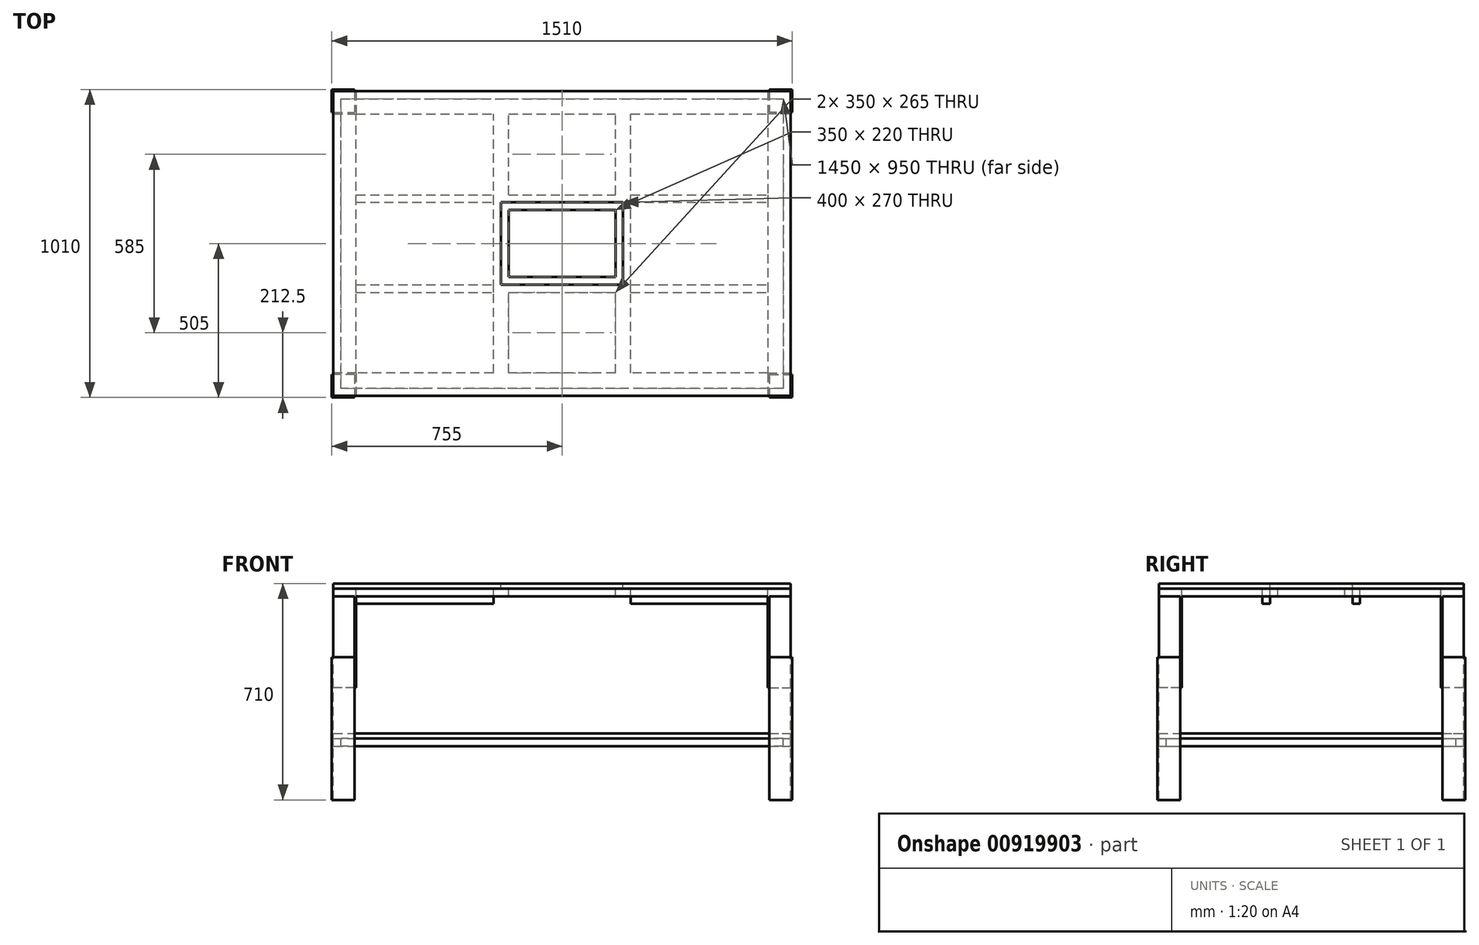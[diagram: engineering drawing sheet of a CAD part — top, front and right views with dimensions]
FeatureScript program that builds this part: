
annotation { "Feature Type Name" : "Feature", "Feature Type Description" : "" }
export const myFeature = defineFeature(function(context is Context, id is Id, definition is map)
    precondition{}
    {
        {
            var Q0;
            Q0=qCreatedBy(makeId("Top.planeOp"),FACE);
            var sketch = newSketch(context, id + "F0", { "sketchPlane" : qUnion([Q0])});
            skLineSegment(sketch, "E0.bottom", {"start": v(750, 500) * mm, "end": v(-750, 500) * mm});
            skLineSegment(sketch, "E0.top", {"start": v(750, -500) * mm, "end": v(-750, -500) * mm});
            skLineSegment(sketch, "E0.left", {"start": v(750, 500) * mm, "end": v(750, -500) * mm});
            skLineSegment(sketch, "E0.right", {"start": v(-750, 500) * mm, "end": v(-750, -500) * mm});
            skPoint(sketch, "E0.middle", {"position": v(0, 0) * mm});
            skSolve(sketch);
        }
        {
            var Q0;
            Q0=makeQuery(id+"F0.imprint","IMPRINT",FACE,{"disambiguationData":[TD([[makeQuery(id+"F0.imprint","IMPRINT",EDGE,{"derivedFrom":sQuery(id+"F0.wireOp",EDGE,"E0.bottom")}),1.0]])]});
            extrude(context, id + "F1", {"entities" : qUnion([Q0]), "depth" : 17 * mm, "offsetDistance" : 25 * mm});
        }
        {
            var Q0;
            Q0=makeQuery(id+"F1.opExtrude","CAP_FACE",FACE,{"disambiguationData":[OSD([sQuery(id+"F0.wireOp",EDGE,"E0.bottom"),sQuery(id+"F0.wireOp",EDGE,"E0.top"),sQuery(id+"F0.wireOp",EDGE,"E0.left"),sQuery(id+"F0.wireOp",EDGE,"E0.right")])],"isStart":true});
            var sketch = newSketch(context, id + "F2", { "sketchPlane" : qUnion([Q0])});
            skLineSegment(sketch, "E1.0.0", {"start": v(750, 500) * mm, "end": v(-750, 500) * mm});
            skLineSegment(sketch, "E1.0.1", {"start": v(-750, 500) * mm, "end": v(-750, -500) * mm});
            skLineSegment(sketch, "E1.0.2", {"start": v(-750, -500) * mm, "end": v(750, -500) * mm});
            skLineSegment(sketch, "E1.0.3", {"start": v(750, -500) * mm, "end": v(750, 500) * mm});
            skLineSegment(sketch, "E2.0", {"start": v(675, 425) * mm, "end": v(-675, 425) * mm});
            skLineSegment(sketch, "E2.1", {"start": v(675, -425) * mm, "end": v(675, 425) * mm});
            skLineSegment(sketch, "E2.2", {"start": v(-675, -425) * mm, "end": v(675, -425) * mm});
            skLineSegment(sketch, "E2.3", {"start": v(-675, 425) * mm, "end": v(-675, -425) * mm});
            skLineSegment(sketch, "E3", {"start": v(-175, 425) * mm, "end": v(-175, -425) * mm});
            skLineSegment(sketch, "E4", {"start": v(175, 425) * mm, "end": v(175, -425) * mm});
            skLineSegment(sketch, "E5", {"start": v(0, 425) * mm, "end": v(0, -425) * mm, "construction": true});
            skLineSegment(sketch, "E6", {"start": v(-675, 0) * mm, "end": v(675, 0) * mm, "construction": true});
            skLineSegment(sketch, "E7.0", {"start": v(225, 425) * mm, "end": v(225, -425) * mm});
            skLineSegment(sketch, "E8.0", {"start": v(-225, 425) * mm, "end": v(-225, -425) * mm});
            skLineSegment(sketch, "E9", {"start": v(-175, 110) * mm, "end": v(175, 110) * mm});
            skLineSegment(sketch, "E10", {"start": v(-175, -110) * mm, "end": v(175, -110) * mm});
            skLineSegment(sketch, "E11.0", {"start": v(-175, 160) * mm, "end": v(175, 160) * mm});
            skLineSegment(sketch, "E12.0", {"start": v(-175, -160) * mm, "end": v(175, -160) * mm});
            skLineSegment(sketch, "E13", {"start": v(-675, 160) * mm, "end": v(-225, 160) * mm});
            skLineSegment(sketch, "E14", {"start": v(-675, -160) * mm, "end": v(-225, -160) * mm});
            skLineSegment(sketch, "E15.0", {"start": v(-675, 135) * mm, "end": v(-225, 135) * mm});
            skLineSegment(sketch, "E16.0", {"start": v(-675, -135) * mm, "end": v(-225, -135) * mm});
            skLineSegment(sketch, "E17.trimOffspring", {"start": v(225, 160) * mm, "end": v(675, 160) * mm});
            skLineSegment(sketch, "E18.trimOffspring", {"start": v(225, 135) * mm, "end": v(675, 135) * mm});
            skLineSegment(sketch, "E19.trimOffspring", {"start": v(225, -135) * mm, "end": v(675, -135) * mm});
            skLineSegment(sketch, "E20.trimOffspring", {"start": v(225, -160) * mm, "end": v(675, -160) * mm});
            skSolve(sketch);
        }
        {
            var Q0;
            Q0=makeQuery(id+"F2.imprint","IMPRINT",FACE,{"disambiguationData":[TD([[makeQuery(id+"F2.imprint","IMPRINT",EDGE,{"derivedFrom":sQuery(id+"F2.wireOp",EDGE,"E1.0.0")}),1.0]])]});
            var Q1;
            {var subQ3=sQuery(id+"F2.wireOp",EDGE,"E2.0");var subQ6=sQuery(id+"F2.wireOp",EDGE,"E3");var subQ11=makeQuery(id+"F2.imprint","INTERSECT",VERTEX,{"derivedFrom":[subQ3,subQ6]});Q1=makeQuery(id+"F2.imprint","IMPRINT",FACE,{"disambiguationData":[TD([[makeQuery(id+"F2.imprint","IMPRINT",EDGE,{"disambiguationData":[TD([[subQ11,-1.0]])],"derivedFrom":subQ3}),1.0]])]});}
            var Q2;
            {var subQ4=sQuery(id+"F2.wireOp",EDGE,"E2.0");var subQ6=sQuery(id+"F2.wireOp",EDGE,"E4");var subQ12=makeQuery(id+"F2.imprint","INTERSECT",VERTEX,{"derivedFrom":[subQ4,subQ6]});Q2=makeQuery(id+"F2.imprint","IMPRINT",FACE,{"disambiguationData":[TD([[makeQuery(id+"F2.imprint","IMPRINT",EDGE,{"disambiguationData":[TD([[subQ12,1.0]])],"derivedFrom":subQ4}),1.0]])]});}
            var Q3;
            {var subQ0=sQuery(id+"F2.wireOp",EDGE,"E9");Q3=makeQuery(id+"F2.imprint","IMPRINT",FACE,{"disambiguationData":[TD([[makeQuery(id+"F2.imprint","IMPRINT",EDGE,{"derivedFrom":subQ0}),1.0]])]});}
            var Q4;
            {var subQ0=sQuery(id+"F2.wireOp",EDGE,"E10");Q4=makeQuery(id+"F2.imprint","IMPRINT",FACE,{"disambiguationData":[TD([[makeQuery(id+"F2.imprint","IMPRINT",EDGE,{"derivedFrom":subQ0}),-1.0]])]});}
            extrude(context, id + "F3", {"entities" : qUnion([Q0, Q1, Q2, Q3, Q4]), "depth" : 25 * mm, "offsetDistance" : 25 * mm});
        }
        {
            var Q0;
            {var subQ0=sQuery(id+"F2.wireOp",EDGE,"E13");Q0=makeQuery(id+"F2.imprint","IMPRINT",FACE,{"disambiguationData":[TD([[makeQuery(id+"F2.imprint","IMPRINT",EDGE,{"derivedFrom":subQ0}),-1.0]])]});}
            var Q1;
            {var subQ0=sQuery(id+"F2.wireOp",EDGE,"E14");Q1=makeQuery(id+"F2.imprint","IMPRINT",FACE,{"disambiguationData":[TD([[makeQuery(id+"F2.imprint","IMPRINT",EDGE,{"derivedFrom":subQ0}),1.0]])]});}
            var Q2;
            {var subQ0=sQuery(id+"F2.wireOp",EDGE,"E17.trimOffspring");Q2=makeQuery(id+"F2.imprint","IMPRINT",FACE,{"disambiguationData":[TD([[makeQuery(id+"F2.imprint","IMPRINT",EDGE,{"derivedFrom":subQ0}),-1.0]])]});}
            var Q3;
            {var subQ0=sQuery(id+"F2.wireOp",EDGE,"E19.trimOffspring");Q3=makeQuery(id+"F2.imprint","IMPRINT",FACE,{"disambiguationData":[TD([[makeQuery(id+"F2.imprint","IMPRINT",EDGE,{"derivedFrom":subQ0}),-1.0]])]});}
            extrude(context, id + "F4", {"entities" : qUnion([Q0, Q1, Q2, Q3]), "depth" : 50 * mm, "offsetDistance" : 25 * mm});
        }
        {
            var Q0;
            Q0=makeQuery(id+"F1.opExtrude","CAP_FACE",FACE,{"disambiguationData":[OSD([sQuery(id+"F0.wireOp",EDGE,"E0.bottom"),sQuery(id+"F0.wireOp",EDGE,"E0.top"),sQuery(id+"F0.wireOp",EDGE,"E0.left"),sQuery(id+"F0.wireOp",EDGE,"E0.right")])],"isStart":false});
            var sketch = newSketch(context, id + "F5", { "sketchPlane" : qUnion([Q0])});
            skLineSegment(sketch, "E21.bottom", {"start": v(200, 135) * mm, "end": v(-200, 135) * mm});
            skLineSegment(sketch, "E21.top", {"start": v(200, -135) * mm, "end": v(-200, -135) * mm});
            skLineSegment(sketch, "E21.left", {"start": v(200, 135) * mm, "end": v(200, -135) * mm});
            skLineSegment(sketch, "E21.right", {"start": v(-200, 135) * mm, "end": v(-200, -135) * mm});
            skPoint(sketch, "E21.middle", {"position": v(0, 0) * mm});
            skSolve(sketch);
        }
        {
            var Q0;
            Q0=makeQuery(id+"F5.imprint","IMPRINT",FACE,{"disambiguationData":[TD([[makeQuery(id+"F5.imprint","IMPRINT",EDGE,{"derivedFrom":sQuery(id+"F5.wireOp",EDGE,"E21.bottom")}),1.0]])]});
            var Q1;
            {var subQ0=sQuery(id+"F2.wireOp",EDGE,"E2.1");Q1=makeQuery(id+"F3.boolean.opBoolean","SPLIT",FACE,{"disambiguationData":[TD([makeQuery(id+"F3.opExtrude","SWEPT_FACE",FACE,{"disambiguationData":[OSD([subQ0])]})])],"derivedFrom":makeQuery(id+"F1.opExtrude","CAP_FACE",FACE,{"disambiguationData":[OSD([sQuery(id+"F0.wireOp",EDGE,"E0.bottom"),sQuery(id+"F0.wireOp",EDGE,"E0.top"),sQuery(id+"F0.wireOp",EDGE,"E0.left"),sQuery(id+"F0.wireOp",EDGE,"E0.right")])],"isStart":true})});}
            extrude(context, id + "F6", {"entities" : qUnion([Q0]), "operationType" : NewBodyOperationType.REMOVE, "endBound" : BoundingType.UP_TO_SURFACE, "oppositeDirection" : true, "depth" : 25 * mm, "endBoundEntityFace" : qUnion([Q1]), "offsetDistance" : 25 * mm});
        }
        {
            var Q0;
            Q0=makeQuery(id+"F3.opExtrude","CAP_FACE",FACE,{"disambiguationData":[OSD([sQuery(id+"F2.wireOp",EDGE,"E1.0.0"),sQuery(id+"F2.wireOp",EDGE,"E1.0.1"),sQuery(id+"F2.wireOp",EDGE,"E1.0.2"),sQuery(id+"F2.wireOp",EDGE,"E1.0.3"),sQuery(id+"F2.wireOp",EDGE,"E2.0"),sQuery(id+"F2.wireOp",EDGE,"E2.1"),sQuery(id+"F2.wireOp",EDGE,"E2.2"),sQuery(id+"F2.wireOp",EDGE,"E2.3"),sQuery(id+"F2.wireOp",EDGE,"E3"),sQuery(id+"F2.wireOp",EDGE,"E4"),sQuery(id+"F2.wireOp",EDGE,"E7.0"),sQuery(id+"F2.wireOp",EDGE,"E8.0"),sQuery(id+"F2.wireOp",EDGE,"E9"),sQuery(id+"F2.wireOp",EDGE,"E10"),sQuery(id+"F2.wireOp",EDGE,"E11.0"),sQuery(id+"F2.wireOp",EDGE,"E12.0")])],"isStart":false});
            var sketch = newSketch(context, id + "F7", { "sketchPlane" : qUnion([Q0])});
            skLineSegment(sketch, "E22.bottom", {"start": v(-675, 425) * mm, "end": v(-750, 425) * mm});
            skLineSegment(sketch, "E22.top", {"start": v(-675, 500) * mm, "end": v(-750, 500) * mm});
            skLineSegment(sketch, "E22.left", {"start": v(-675, 425) * mm, "end": v(-675, 500) * mm});
            skLineSegment(sketch, "E22.right", {"start": v(-750, 425) * mm, "end": v(-750, 500) * mm});
            skLineSegment(sketch, "E23.bottom", {"start": v(675, 425) * mm, "end": v(750, 425) * mm});
            skLineSegment(sketch, "E23.top", {"start": v(675, 500) * mm, "end": v(750, 500) * mm});
            skLineSegment(sketch, "E23.left", {"start": v(675, 425) * mm, "end": v(675, 500) * mm});
            skLineSegment(sketch, "E23.right", {"start": v(750, 425) * mm, "end": v(750, 500) * mm});
            skLineSegment(sketch, "E24.bottom", {"start": v(-750, -500) * mm, "end": v(-675, -500) * mm});
            skLineSegment(sketch, "E24.top", {"start": v(-750, -425) * mm, "end": v(-675, -425) * mm});
            skLineSegment(sketch, "E24.left", {"start": v(-750, -500) * mm, "end": v(-750, -425) * mm});
            skLineSegment(sketch, "E24.right", {"start": v(-675, -500) * mm, "end": v(-675, -425) * mm});
            skLineSegment(sketch, "E25.bottom", {"start": v(750, -500) * mm, "end": v(675, -500) * mm});
            skLineSegment(sketch, "E25.top", {"start": v(750, -425) * mm, "end": v(675, -425) * mm});
            skLineSegment(sketch, "E25.left", {"start": v(750, -500) * mm, "end": v(750, -425) * mm});
            skLineSegment(sketch, "E25.right", {"start": v(675, -500) * mm, "end": v(675, -425) * mm});
            skLineSegment(sketch, "E26.0", {"start": v(-680, 430) * mm, "end": v(-680, 500) * mm});
            skLineSegment(sketch, "E26.1", {"start": v(-680, 430) * mm, "end": v(-750, 430) * mm});
            skLineSegment(sketch, "E27.0", {"start": v(680, 430) * mm, "end": v(680, 500) * mm});
            skLineSegment(sketch, "E27.1", {"start": v(680, 430) * mm, "end": v(750, 430) * mm});
            skLineSegment(sketch, "E28.0", {"start": v(680, -500) * mm, "end": v(680, -430) * mm});
            skLineSegment(sketch, "E28.1", {"start": v(750, -430) * mm, "end": v(680, -430) * mm});
            skLineSegment(sketch, "E29.0", {"start": v(-680, -500) * mm, "end": v(-680, -430) * mm});
            skLineSegment(sketch, "E29.1", {"start": v(-750, -430) * mm, "end": v(-680, -430) * mm});
            skSolve(sketch);
        }
        {
            var Q0;
            {var subQ1=sQuery(id+"F7.wireOp",EDGE,"E24.top");Q0=makeQuery(id+"F7.imprint","IMPRINT",FACE,{"disambiguationData":[TD([[makeQuery(id+"F7.imprint","IMPRINT",EDGE,{"derivedFrom":subQ1}),-1.0]])]});}
            var Q1;
            {var subQ1=sQuery(id+"F7.wireOp",EDGE,"E22.bottom");Q1=makeQuery(id+"F7.imprint","IMPRINT",FACE,{"disambiguationData":[TD([[makeQuery(id+"F7.imprint","IMPRINT",EDGE,{"derivedFrom":subQ1}),-1.0]])]});}
            var Q2;
            {var subQ1=sQuery(id+"F7.wireOp",EDGE,"E23.bottom");Q2=makeQuery(id+"F7.imprint","IMPRINT",FACE,{"disambiguationData":[TD([[makeQuery(id+"F7.imprint","IMPRINT",EDGE,{"derivedFrom":subQ1}),1.0]])]});}
            var Q3;
            {var subQ2=sQuery(id+"F7.wireOp",EDGE,"E25.top");Q3=makeQuery(id+"F7.imprint","IMPRINT",FACE,{"disambiguationData":[TD([[makeQuery(id+"F7.imprint","IMPRINT",EDGE,{"derivedFrom":subQ2}),1.0]])]});}
            extrude(context, id + "F8", {"entities" : qUnion([Q0, Q1, Q2, Q3]), "operationType" : NewBodyOperationType.ADD, "depth" : 300 * mm, "offsetDistance" : 25 * mm});
        }
        {
            var Q0;
            Q0=makeQuery(id+"F8.opExtrude","CAP_FACE",FACE,{"disambiguationData":[OSD([sQuery(id+"F7.wireOp",EDGE,"E23.bottom"),sQuery(id+"F7.wireOp",EDGE,"E23.top"),sQuery(id+"F7.wireOp",EDGE,"E23.left"),sQuery(id+"F7.wireOp",EDGE,"E23.right"),sQuery(id+"F7.wireOp",EDGE,"E27.0"),sQuery(id+"F7.wireOp",EDGE,"E27.1")])],"isStart":false});
            cPlane(context, id + "F9", {"entities" : qUnion([Q0]), "cplaneType" : CPlaneType.OFFSET, "offset" : 100 * mm, "oppositeDirection" : true, "width" : 150 * mm, "height" : 150 * mm});
        }
        {
            var Q0;
            Q0=qCreatedBy(id+"F9.planeOp",FACE);
            var sketch = newSketch(context, id + "F10", { "sketchPlane" : qUnion([Q0])});
            skLineSegment(sketch, "E30.0.0", {"start": v(750, 430) * mm, "end": v(680, 430) * mm});
            skLineSegment(sketch, "E30.0.1", {"start": v(680, 430) * mm, "end": v(680, 500) * mm});
            skLineSegment(sketch, "E30.0.2", {"start": v(680, 500) * mm, "end": v(675, 500) * mm});
            skLineSegment(sketch, "E30.0.3", {"start": v(675, 500) * mm, "end": v(675, 425) * mm});
            skLineSegment(sketch, "E30.0.4", {"start": v(675, 425) * mm, "end": v(750, 425) * mm});
            skLineSegment(sketch, "E30.0.5", {"start": v(750, 425) * mm, "end": v(750, 430) * mm});
            skLineSegment(sketch, "E31", {"start": v(680, 500) * mm, "end": v(750, 500) * mm});
            skLineSegment(sketch, "E32", {"start": v(750, 500) * mm, "end": v(750, 430) * mm});
            skLineSegment(sketch, "E33", {"start": v(750, 430) * mm, "end": v(755, 430) * mm});
            skLineSegment(sketch, "E34", {"start": v(755, 430) * mm, "end": v(755, 505) * mm});
            skLineSegment(sketch, "E35", {"start": v(755, 505) * mm, "end": v(680, 505) * mm});
            skLineSegment(sketch, "E36", {"start": v(680, 505) * mm, "end": v(680, 500) * mm});
            skLineSegment(sketch, "E37.0.0", {"start": v(-680, 500) * mm, "end": v(-680, 430) * mm});
            skLineSegment(sketch, "E37.0.1", {"start": v(-680, 430) * mm, "end": v(-750, 430) * mm});
            skLineSegment(sketch, "E37.0.2", {"start": v(-750, 430) * mm, "end": v(-750, 425) * mm});
            skLineSegment(sketch, "E37.0.3", {"start": v(-750, 425) * mm, "end": v(-675, 425) * mm});
            skLineSegment(sketch, "E37.0.4", {"start": v(-675, 425) * mm, "end": v(-675, 500) * mm});
            skLineSegment(sketch, "E37.0.5", {"start": v(-675, 500) * mm, "end": v(-680, 500) * mm});
            skPoint(sketch, "E38.0", {"position": v(-750, 500) * mm});
            skLineSegment(sketch, "E39", {"start": v(-680, 500) * mm, "end": v(-750, 500) * mm});
            skLineSegment(sketch, "E40", {"start": v(-750, 500) * mm, "end": v(-750, 430) * mm});
            skLineSegment(sketch, "E41", {"start": v(-750, 430) * mm, "end": v(-755, 430) * mm});
            skLineSegment(sketch, "E42", {"start": v(-755, 430) * mm, "end": v(-755, 505) * mm});
            skLineSegment(sketch, "E43", {"start": v(-755, 505) * mm, "end": v(-680, 505) * mm});
            skLineSegment(sketch, "E44", {"start": v(-680, 505) * mm, "end": v(-680, 500) * mm});
            skLineSegment(sketch, "E45", {"start": v(-750, 500) * mm, "end": v(-680, 500) * mm});
            skLineSegment(sketch, "E46.0.0", {"start": v(-750, -425) * mm, "end": v(-750, -430) * mm});
            skLineSegment(sketch, "E46.0.1", {"start": v(-750, -430) * mm, "end": v(-680, -430) * mm});
            skLineSegment(sketch, "E46.0.2", {"start": v(-680, -430) * mm, "end": v(-680, -500) * mm});
            skLineSegment(sketch, "E46.0.3", {"start": v(-680, -500) * mm, "end": v(-675, -500) * mm});
            skLineSegment(sketch, "E46.0.4", {"start": v(-675, -500) * mm, "end": v(-675, -425) * mm});
            skLineSegment(sketch, "E46.0.5", {"start": v(-675, -425) * mm, "end": v(-750, -425) * mm});
            skPoint(sketch, "E47.0", {"position": v(-750, -500) * mm});
            skLineSegment(sketch, "E48", {"start": v(-750, -430) * mm, "end": v(-750, -500) * mm});
            skLineSegment(sketch, "E49", {"start": v(-750, -500) * mm, "end": v(-680, -500) * mm});
            skLineSegment(sketch, "E50", {"start": v(-680, -500) * mm, "end": v(-680, -505) * mm});
            skLineSegment(sketch, "E51", {"start": v(-680, -505) * mm, "end": v(-755, -505) * mm});
            skLineSegment(sketch, "E52", {"start": v(-755, -505) * mm, "end": v(-755, -430) * mm});
            skLineSegment(sketch, "E53", {"start": v(-755, -430) * mm, "end": v(-750, -430) * mm});
            skLineSegment(sketch, "E54.0.0", {"start": v(680, -430) * mm, "end": v(750, -430) * mm});
            skLineSegment(sketch, "E54.0.1", {"start": v(750, -430) * mm, "end": v(750, -425) * mm});
            skLineSegment(sketch, "E54.0.2", {"start": v(750, -425) * mm, "end": v(675, -425) * mm});
            skLineSegment(sketch, "E54.0.3", {"start": v(675, -425) * mm, "end": v(675, -500) * mm});
            skLineSegment(sketch, "E54.0.4", {"start": v(675, -500) * mm, "end": v(680, -500) * mm});
            skLineSegment(sketch, "E54.0.5", {"start": v(680, -500) * mm, "end": v(680, -430) * mm});
            skPoint(sketch, "E55.0", {"position": v(750, -500) * mm});
            skLineSegment(sketch, "E56", {"start": v(750, -430) * mm, "end": v(750, -500) * mm});
            skLineSegment(sketch, "E57", {"start": v(750, -500) * mm, "end": v(680, -500) * mm});
            skLineSegment(sketch, "E58", {"start": v(680, -500) * mm, "end": v(680, -505) * mm});
            skLineSegment(sketch, "E59", {"start": v(680, -505) * mm, "end": v(755, -505) * mm});
            skLineSegment(sketch, "E60", {"start": v(755, -505) * mm, "end": v(755, -430) * mm});
            skLineSegment(sketch, "E61", {"start": v(755, -430) * mm, "end": v(750, -430) * mm});
            skSolve(sketch);
        }
        {
            var Q0;
            Q0=makeQuery(id+"F10.imprint","IMPRINT",FACE,{"disambiguationData":[TD([[makeQuery(id+"F10.imprint","IMPRINT",EDGE,{"derivedFrom":sQuery(id+"F10.wireOp",EDGE,"E56")}),1.0]])]});
            var Q1;
            Q1=makeQuery(id+"F10.imprint","IMPRINT",FACE,{"disambiguationData":[TD([[makeQuery(id+"F10.imprint","IMPRINT",EDGE,{"derivedFrom":sQuery(id+"F10.wireOp",EDGE,"E31")}),1.0]])]});
            var Q2;
            Q2=makeQuery(id+"F10.imprint","IMPRINT",FACE,{"disambiguationData":[TD([[makeQuery(id+"F10.imprint","IMPRINT",EDGE,{"derivedFrom":sQuery(id+"F10.wireOp",EDGE,"E41")}),-1.0]])]});
            var Q3;
            Q3=makeQuery(id+"F10.imprint","IMPRINT",FACE,{"disambiguationData":[TD([[makeQuery(id+"F10.imprint","IMPRINT",EDGE,{"derivedFrom":sQuery(id+"F10.wireOp",EDGE,"E48")}),-1.0]])]});
            extrude(context, id + "F11", {"entities" : qUnion([Q0, Q1, Q2, Q3]), "operationType" : NewBodyOperationType.ADD, "depth" : 468 * mm, "offsetDistance" : 25 * mm});
        }
        {
            var Q0;
            {var subQ4=sQuery(id+"F7.wireOp",EDGE,"E22.left");Q0=makeQuery(id+"F7.imprint","IMPRINT",FACE,{"disambiguationData":[TD([[makeQuery(id+"F7.imprint","IMPRINT",EDGE,{"derivedFrom":subQ4}),-1.0]])]});}
            cPlane(context, id + "F12", {"entities" : qUnion([Q0]), "cplaneType" : CPlaneType.OFFSET, "offset" : 450 * mm, "width" : 150 * mm, "height" : 150 * mm});
        }
        {
            var Q0;
            Q0=qCreatedBy(id+"F12.planeOp",FACE);
            var sketch = newSketch(context, id + "F13", { "sketchPlane" : qUnion([Q0])});
            skPoint(sketch, "E62.0", {"position": v(-750, 500) * mm});
            skPoint(sketch, "E63.0", {"position": v(750, -500) * mm});
            skLineSegment(sketch, "E64.bottom", {"start": v(-750, 500) * mm, "end": v(750, 500) * mm});
            skLineSegment(sketch, "E64.top", {"start": v(-750, -500) * mm, "end": v(750, -500) * mm});
            skLineSegment(sketch, "E64.left", {"start": v(-750, 500) * mm, "end": v(-750, -500) * mm});
            skLineSegment(sketch, "E64.right", {"start": v(750, 500) * mm, "end": v(750, -500) * mm});
            skSolve(sketch);
        }
        {
            var Q0;
            Q0=makeQuery(id+"F13.imprint","IMPRINT",FACE,{"disambiguationData":[TD([[makeQuery(id+"F13.imprint","IMPRINT",EDGE,{"derivedFrom":sQuery(id+"F13.wireOp",EDGE,"E64.bottom")}),-1.0]])]});
            extrude(context, id + "F14", {"entities" : qUnion([Q0]), "depth" : 17 * mm, "offsetDistance" : 25 * mm});
        }
        {
            var Q0;
            Q0=makeQuery(id+"F14.opExtrude","CAP_FACE",FACE,{"disambiguationData":[OSD([sQuery(id+"F13.wireOp",EDGE,"E64.bottom"),sQuery(id+"F13.wireOp",EDGE,"E64.top"),sQuery(id+"F13.wireOp",EDGE,"E64.left"),sQuery(id+"F13.wireOp",EDGE,"E64.right")])],"isStart":false});
            var sketch = newSketch(context, id + "F15", { "sketchPlane" : qUnion([Q0])});
            skLineSegment(sketch, "E65.bottom", {"start": v(-750, 500) * mm, "end": v(750, 500) * mm});
            skLineSegment(sketch, "E65.top", {"start": v(-750, -500) * mm, "end": v(750, -500) * mm});
            skLineSegment(sketch, "E65.left", {"start": v(-750, 500) * mm, "end": v(-750, -500) * mm});
            skLineSegment(sketch, "E65.right", {"start": v(750, 500) * mm, "end": v(750, -500) * mm});
            skLineSegment(sketch, "E66.0", {"start": v(-725, 475) * mm, "end": v(-725, -475) * mm});
            skLineSegment(sketch, "E66.1", {"start": v(725, 475) * mm, "end": v(-725, 475) * mm});
            skLineSegment(sketch, "E66.2", {"start": v(725, -475) * mm, "end": v(725, 475) * mm});
            skLineSegment(sketch, "E66.3", {"start": v(-725, -475) * mm, "end": v(725, -475) * mm});
            skSolve(sketch);
        }
        {
            var Q0;
            Q0=makeQuery(id+"F15.imprint","IMPRINT",FACE,{"disambiguationData":[TD([[makeQuery(id+"F15.imprint","IMPRINT",EDGE,{"derivedFrom":sQuery(id+"F15.wireOp",EDGE,"E65.bottom")}),-1.0]])]});
            extrude(context, id + "F16", {"entities" : qUnion([Q0]), "depth" : 25 * mm, "offsetDistance" : 25 * mm});
        }
    });
